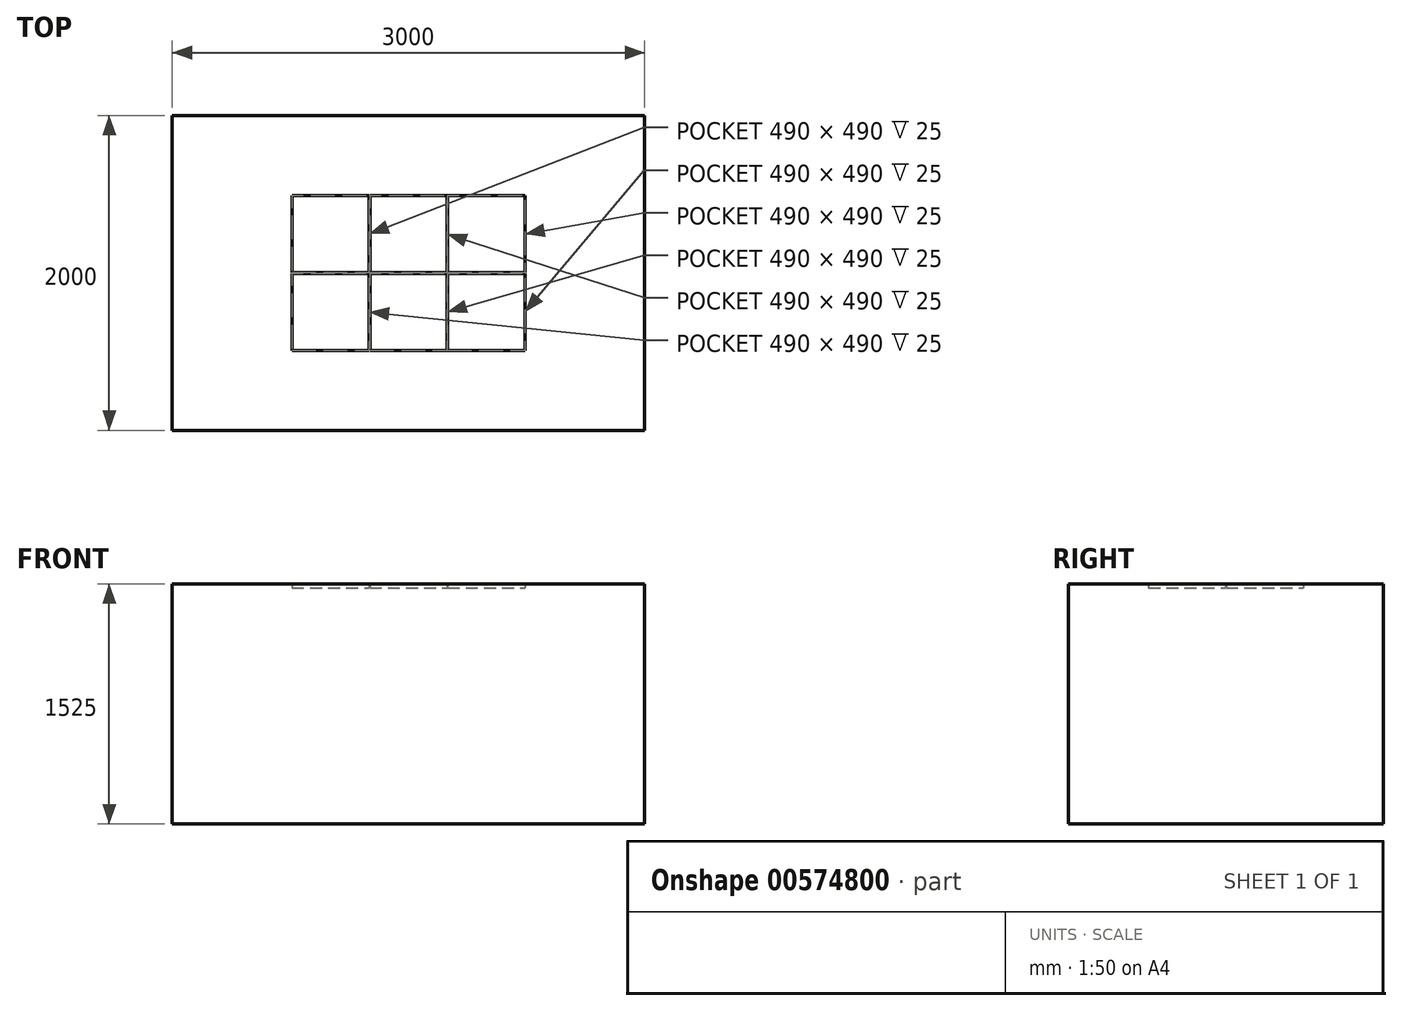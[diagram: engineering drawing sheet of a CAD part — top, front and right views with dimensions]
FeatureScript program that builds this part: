
annotation { "Feature Type Name" : "Feature", "Feature Type Description" : "" }
export const myFeature = defineFeature(function(context is Context, id is Id, definition is map)
    precondition{}
    {
        {
            var Q0;
            Q0=qCreatedBy(makeId("Top.planeOp"),FACE);
            var sketch = newSketch(context, id + "F0", { "sketchPlane" : qUnion([Q0])});
            skLineSegment(sketch, "E0.bottom", {"start": v(-1500, -1000) * mm, "end": v(1500, -1000) * mm});
            skLineSegment(sketch, "E0.top", {"start": v(-1500, 1000) * mm, "end": v(1500, 1000) * mm});
            skLineSegment(sketch, "E0.left", {"start": v(-1500, -1000) * mm, "end": v(-1500, 1000) * mm});
            skLineSegment(sketch, "E0.right", {"start": v(1500, -1000) * mm, "end": v(1500, 1000) * mm});
            skSolve(sketch);
        }
        {
            var Q0;
            Q0=makeQuery(id+"F0.imprint","IMPRINT",FACE,{"disambiguationData":[TD([[makeQuery(id+"F0.imprint","IMPRINT",EDGE,{"derivedFrom":sQuery(id+"F0.wireOp",EDGE,"E0.bottom")}),1.0]])]});
            extrude(context, id + "F1", {"entities" : qUnion([Q0]), "depth" : -1500 * mm, "offsetDistance" : 25 * mm});
        }
        {
            var Q0;
            Q0=makeQuery(id+"F1.opExtrude","CAP_FACE",FACE,{"disambiguationData":[OSD([sQuery(id+"F0.wireOp",EDGE,"E0.bottom"),sQuery(id+"F0.wireOp",EDGE,"E0.top"),sQuery(id+"F0.wireOp",EDGE,"E0.left"),sQuery(id+"F0.wireOp",EDGE,"E0.right")])],"isStart":true});
            var sketch = newSketch(context, id + "F2", { "sketchPlane" : qUnion([Q0])});
            skLineSegment(sketch, "E1.bottom", {"start": v(-740, 2.5) * mm, "end": v(-250, 2.5) * mm});
            skLineSegment(sketch, "E1.top", {"start": v(-740, 492.5) * mm, "end": v(-250, 492.5) * mm});
            skLineSegment(sketch, "E1.left", {"start": v(-740, 2.5) * mm, "end": v(-740, 492.5) * mm});
            skLineSegment(sketch, "E1.right", {"start": v(-250, 2.5) * mm, "end": v(-250, 492.5) * mm});
            skLineSegment(sketch, "E2.0.1.0", {"start": v(-740, -492.5) * mm, "end": v(-250, -492.5) * mm});
            skLineSegment(sketch, "E2.0.1.1", {"start": v(-740, -492.5) * mm, "end": v(-740, -2.5) * mm});
            skLineSegment(sketch, "E2.0.1.2", {"start": v(-250, -492.5) * mm, "end": v(-250, -2.5) * mm});
            skLineSegment(sketch, "E2.0.1.3", {"start": v(-740, -2.5) * mm, "end": v(-250, -2.5) * mm});
            skLineSegment(sketch, "E2.1.0.0", {"start": v(-245, 2.5) * mm, "end": v(245, 2.5) * mm});
            skLineSegment(sketch, "E2.1.0.1", {"start": v(-245, 2.5) * mm, "end": v(-245, 492.5) * mm});
            skLineSegment(sketch, "E2.1.0.2", {"start": v(245, 2.5) * mm, "end": v(245, 492.5) * mm});
            skLineSegment(sketch, "E2.1.0.3", {"start": v(-245, 492.5) * mm, "end": v(245, 492.5) * mm});
            skLineSegment(sketch, "E2.1.1.0", {"start": v(-245, -492.5) * mm, "end": v(245, -492.5) * mm});
            skLineSegment(sketch, "E2.1.1.1", {"start": v(-245, -492.5) * mm, "end": v(-245, -2.5) * mm});
            skLineSegment(sketch, "E2.1.1.2", {"start": v(245, -492.5) * mm, "end": v(245, -2.5) * mm});
            skLineSegment(sketch, "E2.1.1.3", {"start": v(-245, -2.5) * mm, "end": v(245, -2.5) * mm});
            skLineSegment(sketch, "E2.2.0.0", {"start": v(250, 2.5) * mm, "end": v(740, 2.5) * mm});
            skLineSegment(sketch, "E2.2.0.1", {"start": v(250, 2.5) * mm, "end": v(250, 492.5) * mm});
            skLineSegment(sketch, "E2.2.0.2", {"start": v(740, 2.5) * mm, "end": v(740, 492.5) * mm});
            skLineSegment(sketch, "E2.2.0.3", {"start": v(250, 492.5) * mm, "end": v(740, 492.5) * mm});
            skLineSegment(sketch, "E2.2.1.0", {"start": v(250, -492.5) * mm, "end": v(740, -492.5) * mm});
            skLineSegment(sketch, "E2.2.1.1", {"start": v(250, -492.5) * mm, "end": v(250, -2.5) * mm});
            skLineSegment(sketch, "E2.2.1.2", {"start": v(740, -492.5) * mm, "end": v(740, -2.5) * mm});
            skLineSegment(sketch, "E2.2.1.3", {"start": v(250, -2.5) * mm, "end": v(740, -2.5) * mm});
            skLineSegment(sketch, "E2.direction1", {"start": v(-740, 2.5) * mm, "end": v(-245, 2.5) * mm, "construction": true});
            skLineSegment(sketch, "E2.direction2", {"start": v(-740, 2.5) * mm, "end": v(-740, -492.5) * mm, "construction": true});
            skSolve(sketch);
        }
        {
            var Q0;
            Q0=makeQuery(id+"F2.imprint","IMPRINT",FACE,{"disambiguationData":[TD([[makeQuery(id+"F2.imprint","IMPRINT",EDGE,{"derivedFrom":sQuery(id+"F2.wireOp",EDGE,"E1.bottom")}),-1.0]])]});
            extrude(context, id + "F3", {"entities" : qUnion([Q0]), "operationType" : NewBodyOperationType.ADD, "depth" : 25 * mm, "offsetDistance" : 25 * mm});
        }
    });
